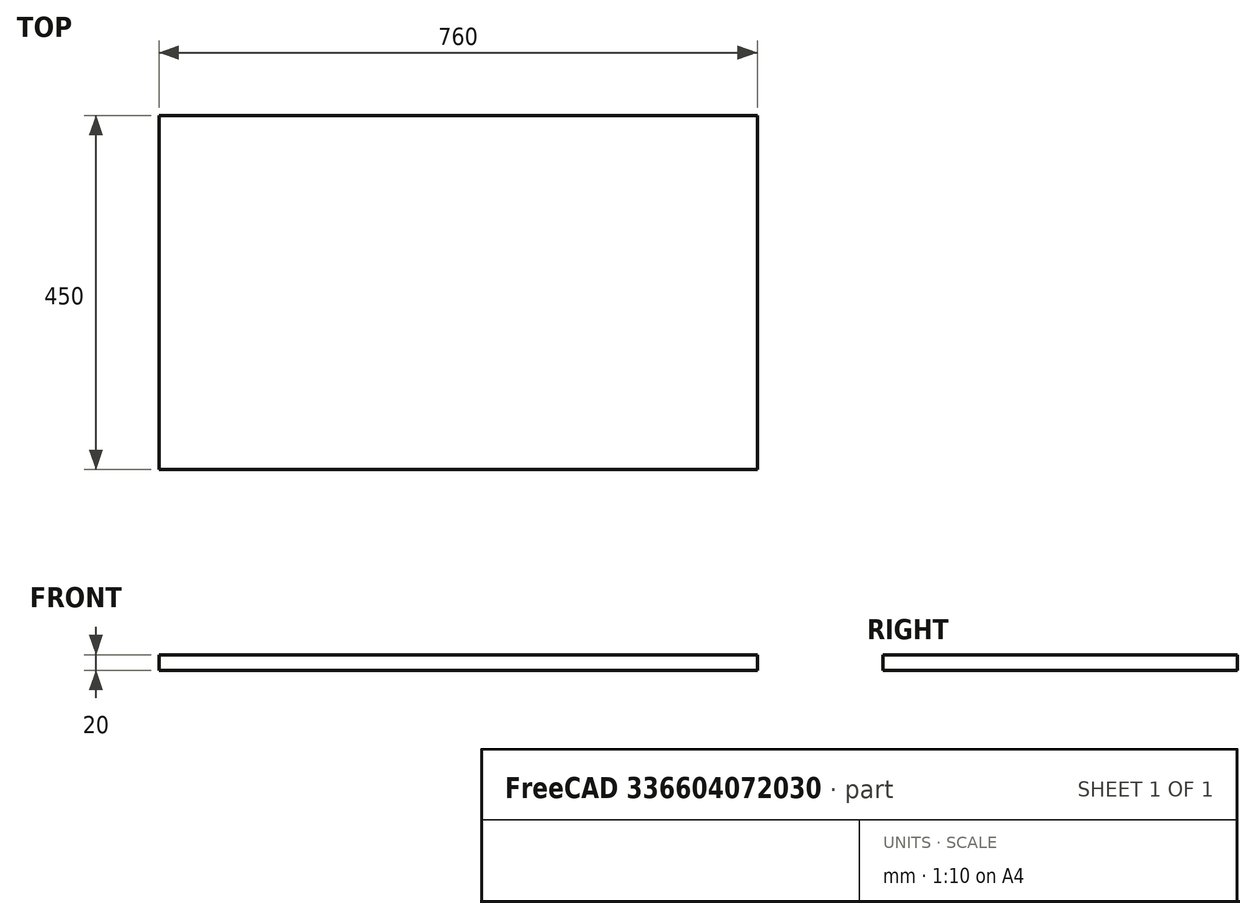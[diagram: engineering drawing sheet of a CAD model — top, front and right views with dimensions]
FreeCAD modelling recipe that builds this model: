
FCSTD DOCUMENT  (FreeCAD 0.20R29603 (Git))
Label: RegalBoden
License: All rights reserved
LicenseURL: http://en.wikipedia.org/wiki/All_rights_reserved
objects: Sketcher::SketchObject×1, PartDesign::Pad×1, PartDesign::Body×1
note: 4 computed .brp shape members not serialized (recipe doc carries the construction recipe); baked Part::Feature solids carry a one-line shape summary decoded from their .brp

FEATURE [Sketcher::SketchObject] Sketch
  FullyConstrained = true
  MapMode = 5
  Support = -> [XY_Plane]
  sketch-geometry (5):
    g0: LineSegment StartX=-380 StartY=225 StartZ=0 EndX=-380 EndY=-225 EndZ=0
    g1: LineSegment StartX=-380 StartY=-225 StartZ=0 EndX=380 EndY=-225 EndZ=0
    g2: LineSegment StartX=380 StartY=-225 StartZ=0 EndX=380 EndY=225 EndZ=0
    g3: LineSegment StartX=380 StartY=225 StartZ=0 EndX=-380 EndY=225 EndZ=0
    g4: GeomPoint X=0 Y=0 Z=0
  constraints (12):
    c: Coincident(g0,g1)
    c: Coincident(g1,g2)
    c: Coincident(g2,g3)
    c: Coincident(g3,g0)
    c: Horizontal(g1)
    c: Horizontal(g3)
    c: Vertical(g0)
    c: Vertical(g2)
    c: Symmetric(g1,g0,g4)
    c: Coincident(g4,g-1)
    c: Distance(g3) = 760
    c: Distance(g0) = 450
FEATURE [PartDesign::Pad] Pad
  Direction = (0,0,1)
  Length = 20
  Length2 = 10
  Profile = -> Sketch
  ReferenceAxis = -> Sketch [N_Axis]
  Type = 0
FEATURE [PartDesign::Body] Body
  Group = -> [Sketch,Pad]
  Origin = -> Origin
  Tip = -> Pad
